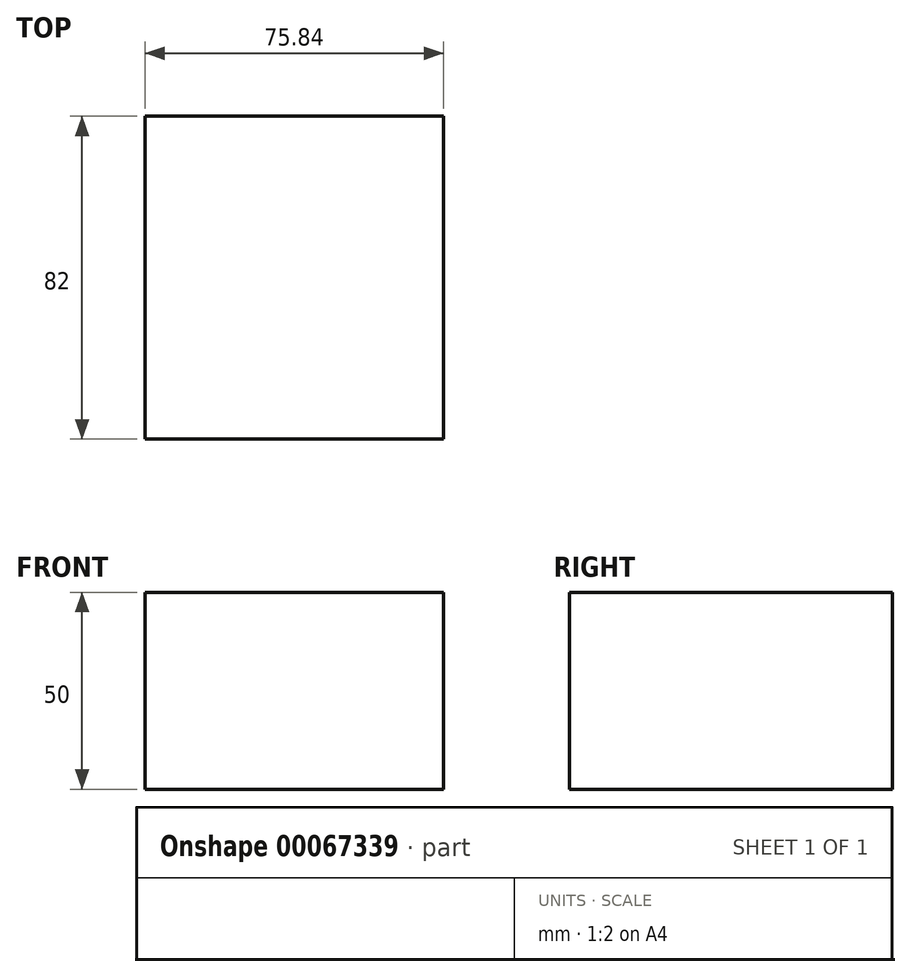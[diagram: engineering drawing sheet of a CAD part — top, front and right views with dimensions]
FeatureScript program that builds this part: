
annotation { "Feature Type Name" : "Feature", "Feature Type Description" : "" }
export const myFeature = defineFeature(function(context is Context, id is Id, definition is map)
    precondition{}
    {
        {
            var Q0;
            Q0=qCreatedBy(makeId("Top.planeOp"),FACE);
            var sketch = newSketch(context, id + "F0", { "sketchPlane" : qUnion([Q0])});
            skLineSegment(sketch, "E0.rect.bottom", {"start": v(37.92, -41) * mm, "end": v(-37.92, -41) * mm});
            skLineSegment(sketch, "E0.rect.top", {"start": v(37.92, 41) * mm, "end": v(-37.92, 41) * mm});
            skLineSegment(sketch, "E0.rect.left", {"start": v(37.92, -41) * mm, "end": v(37.92, 41) * mm});
            skLineSegment(sketch, "E0.rect.right", {"start": v(-37.92, -41) * mm, "end": v(-37.92, 41) * mm});
            skPoint(sketch, "E0.rect.middle", {"position": v(0, 0) * mm});
            skSolve(sketch);
        }
        {
            var Q0;
            Q0=sQuery(id+"F0.wireOp",EDGE,"E0.rect.bottom");
            var Q1;
            Q1=sQuery(id+"F0.wireOp",EDGE,"E0.rect.top");
            var Q2;
            Q2=sQuery(id+"F0.wireOp",EDGE,"E0.rect.left");
            var Q3;
            Q3=sQuery(id+"F0.wireOp",EDGE,"E0.rect.right");
            extrude(context, id + "F1", {"bodyType" : ToolBodyType.SURFACE, "surfaceEntities" : qUnion([Q0, Q1, Q2, Q3]), "depth" : 50 * mm});
        }
    });
